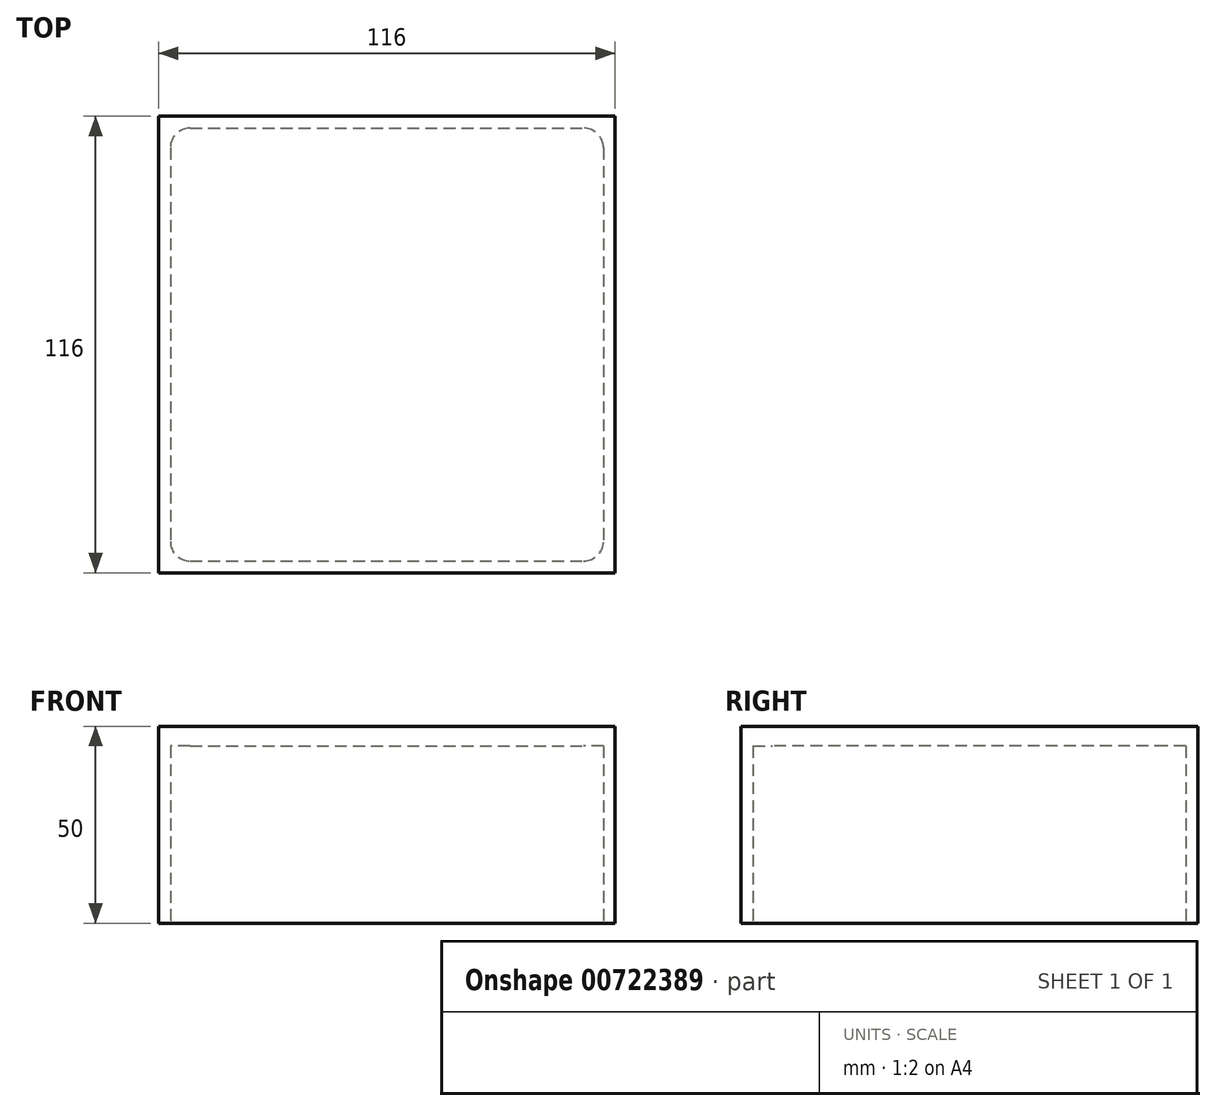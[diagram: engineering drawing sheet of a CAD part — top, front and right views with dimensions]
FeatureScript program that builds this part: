
annotation { "Feature Type Name" : "Feature", "Feature Type Description" : "" }
export const myFeature = defineFeature(function(context is Context, id is Id, definition is map)
    precondition{}
    {
        {
            var Q0;
            Q0=qCreatedBy(makeId("Top.planeOp"),FACE);
            var sketch = newSketch(context, id + "F0", { "sketchPlane" : qUnion([Q0])});
            skLineSegment(sketch, "E0.bottom", {"start": v(-58, 58) * mm, "end": v(58, 58) * mm});
            skLineSegment(sketch, "E0.top", {"start": v(-58, -58) * mm, "end": v(58, -58) * mm});
            skLineSegment(sketch, "E0.left", {"start": v(-58, 58) * mm, "end": v(-58, -58) * mm});
            skLineSegment(sketch, "E0.right", {"start": v(58, 58) * mm, "end": v(58, -58) * mm});
            skPoint(sketch, "E0.middle", {"position": v(0, 0) * mm});
            skSolve(sketch);
        }
        {
            var Q0;
            Q0 = qSketchRegion(id + "F0", true);
            extrude(context, id + "F1", {"entities" : qUnion([Q0]), "depth" : 50 * mm, "offsetDistance" : 25 * mm});
        }
        {
            var Q0;
            Q0=qCreatedBy(makeId("Top.planeOp"),FACE);
            var sketch = newSketch(context, id + "F2", { "sketchPlane" : qUnion([Q0])});
            skLineSegment(sketch, "E1.bottom", {"start": v(-55, 55) * mm, "end": v(55, 55) * mm});
            skLineSegment(sketch, "E1.top", {"start": v(-55, -55) * mm, "end": v(55, -55) * mm});
            skLineSegment(sketch, "E1.left", {"start": v(-55, 55) * mm, "end": v(-55, -55) * mm});
            skLineSegment(sketch, "E1.right", {"start": v(55, 55) * mm, "end": v(55, -55) * mm});
            skPoint(sketch, "E1.middle", {"position": v(0, 0) * mm});
            skSolve(sketch);
        }
        {
            var Q0;
            Q0 = qSketchRegion(id + "F2", true);
            extrude(context, id + "F3", {"entities" : qUnion([Q0]), "operationType" : NewBodyOperationType.REMOVE, "depth" : 45 * mm, "offsetDistance" : 25 * mm});
        }
        {
            var Q0;
            Q0=makeQuery(id+"F3.boolean.opBoolean","COPY",EDGE,{"derivedFrom":makeQuery(id+"F3.opExtrude","SWEPT_EDGE",EDGE,{"disambiguationData":[OSD([sQuery(id+"F2.wireOp",EDGE,"E1.bottom"),sQuery(id+"F2.wireOp",EDGE,"E1.right")])]})});
            var Q1;
            Q1=makeQuery(id+"F3.boolean.opBoolean","COPY",EDGE,{"derivedFrom":makeQuery(id+"F3.opExtrude","SWEPT_EDGE",EDGE,{"disambiguationData":[OSD([sQuery(id+"F2.wireOp",EDGE,"E1.top"),sQuery(id+"F2.wireOp",EDGE,"E1.left")])]})});
            var Q2;
            Q2=makeQuery(id+"F3.boolean.opBoolean","COPY",EDGE,{"derivedFrom":makeQuery(id+"F3.opExtrude","SWEPT_EDGE",EDGE,{"disambiguationData":[OSD([sQuery(id+"F2.wireOp",EDGE,"E1.top"),sQuery(id+"F2.wireOp",EDGE,"E1.right")])]})});
            var Q3;
            Q3=makeQuery(id+"F3.boolean.opBoolean","COPY",EDGE,{"derivedFrom":makeQuery(id+"F3.opExtrude","SWEPT_EDGE",EDGE,{"disambiguationData":[OSD([sQuery(id+"F2.wireOp",EDGE,"E1.bottom"),sQuery(id+"F2.wireOp",EDGE,"E1.left")])]})});
            fillet(context, id + "F4", {"entities" : qUnion([Q0, Q1, Q2, Q3]), "radius" : 5 * mm, "tangentPropagation" : true, "allowEdgeOverflow" : false});
        }
    });
